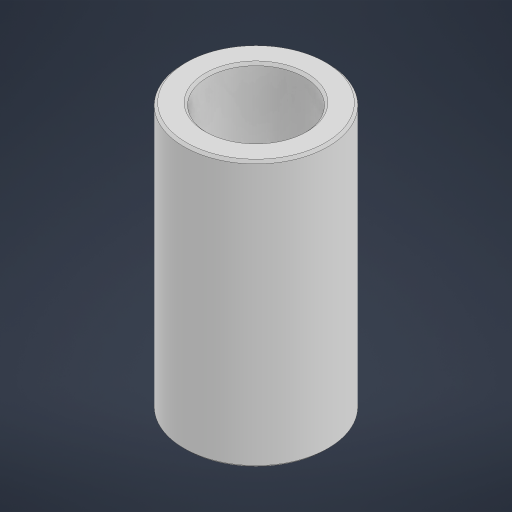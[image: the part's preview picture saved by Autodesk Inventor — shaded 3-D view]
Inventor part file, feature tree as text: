
AUTODESK INVENTOR PART (.ipt)
format: ipt  version: 2023 (Build 270158000, 158)  size: 175,616 bytes
history: native  units: in
note: dims shown in document units (in); Inventor stores cm internally (conversion verified against a paired STEP export)
features: chamfer x1
ambient origin geometry x8: Origin, YZ Plane, XZ Plane, XY Plane, X Axis, Y Axis, Z Axis, Center Point
bodies: Solid1 (feature_tree)
feature tree (1):
  chamfer  "Chamfer1"  [1 undecoded]
note: 1 required parameter value undecoded (feature->parameter linkage not recoverable at this tier; creation-order binding heuristic only, values carry confidence <= 0.55)
